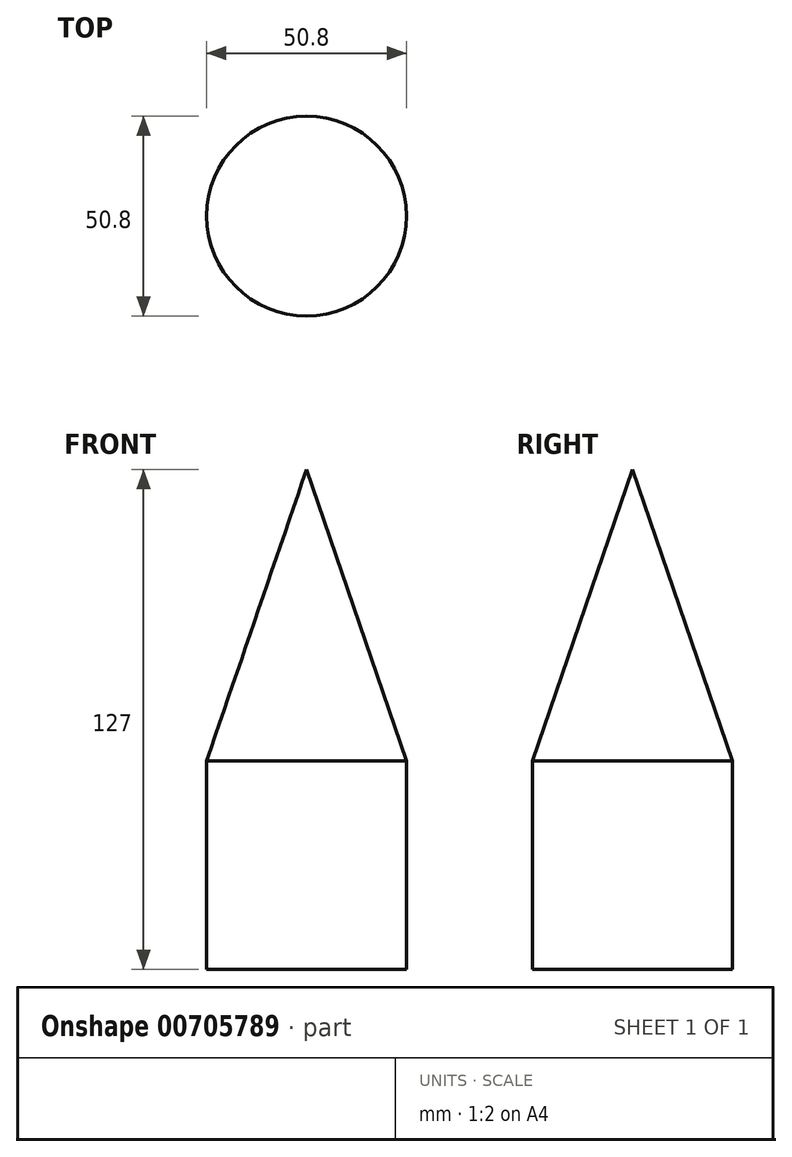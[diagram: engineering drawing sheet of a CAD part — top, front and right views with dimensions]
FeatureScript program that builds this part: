
annotation { "Feature Type Name" : "Feature", "Feature Type Description" : "" }
export const myFeature = defineFeature(function(context is Context, id is Id, definition is map)
    precondition{}
    {
        {
            var Q0;
            Q0=qCreatedBy(makeId("Top.planeOp"),FACE);
            var sketch = newSketch(context, id + "F0", { "sketchPlane" : qUnion([Q0])});
            skCircle(sketch, "E0", {"center": v(0, 0) * mm, "radius": 25.4 * mm});
            skSolve(sketch);
        }
        {
            var Q0;
            Q0=makeQuery(id+"F0.imprint","IMPRINT",FACE,{"disambiguationData":[TD([[makeQuery(id+"F0.imprint","IMPRINT",EDGE,{"derivedFrom":sQuery(id+"F0.wireOp",EDGE,"E0")}),1.0]])]});
            extrude(context, id + "F1", {"entities" : qUnion([Q0]), "depth" : 127 * mm, "offsetDistance" : 25.4 * mm});
        }
        {
            var Q0;
            Q0=qCreatedBy(makeId("Right.planeOp"),FACE);
            var sketch = newSketch(context, id + "F2", { "sketchPlane" : qUnion([Q0])});
            skLineSegment(sketch, "E1", {"start": v(0, 127) * mm, "end": v(32.9, 127) * mm});
            skLineSegment(sketch, "E2", {"start": v(32.9, 127) * mm, "end": v(30.18, 38.97) * mm});
            skLineSegment(sketch, "E3", {"start": v(30.18, 38.97) * mm, "end": v(0, 127) * mm});
            skSolve(sketch);
        }
        {
            var Q0;
            Q0 = qSketchRegion(id + "F2", true);
            var Q1;
            Q1=makeQuery(id+"F1.opExtrude","SWEPT_FACE",FACE,{"disambiguationData":[OSD([sQuery(id+"F0.wireOp",EDGE,"E0")])]});
            revolve(context, id + "F3", {"operationType" : NewBodyOperationType.REMOVE, "surfaceOperationType" : NewSurfaceOperationType.NEW, "entities" : qUnion([Q0]), "axis" : qUnion([Q1]), "revolveType" : RevolveType.FULL});
        }
    });
